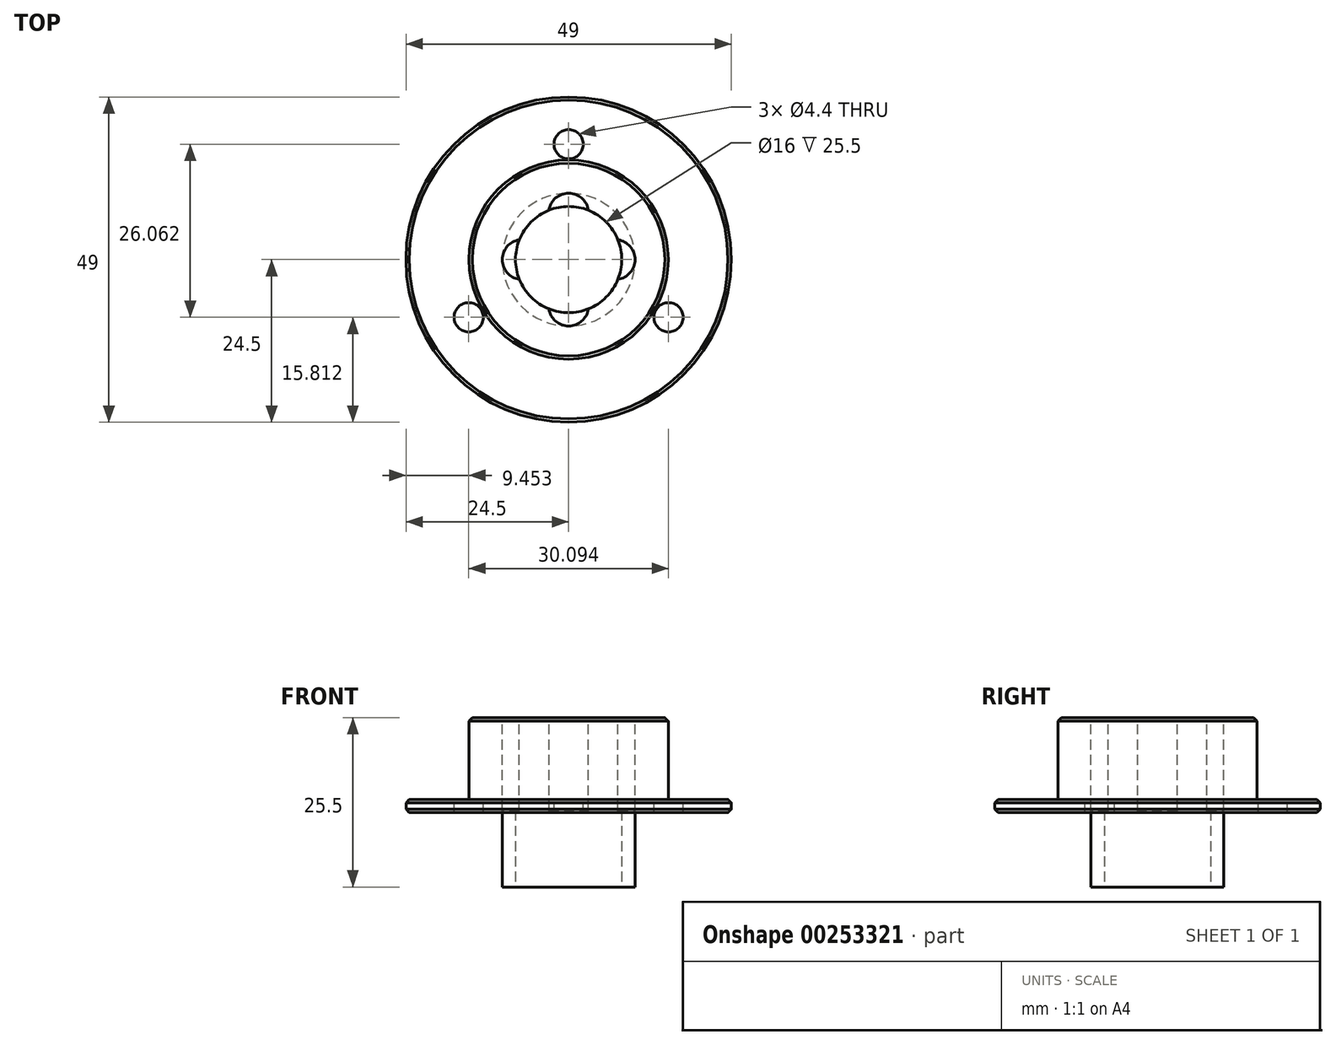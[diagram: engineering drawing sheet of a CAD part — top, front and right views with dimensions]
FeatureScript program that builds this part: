
annotation { "Feature Type Name" : "Feature", "Feature Type Description" : "" }
export const myFeature = defineFeature(function(context is Context, id is Id, definition is map)
    precondition{}
    {
        {
            var Q0;
            Q0=qCreatedBy(makeId("Top.planeOp"),FACE);
            var sketch = newSketch(context, id + "F0", { "sketchPlane" : qUnion([Q0])});
            skCircle(sketch, "E0", {"center": v(0, 0) * mm, "radius": 24.5 * mm});
            skCircle(sketch, "E1", {"center": v(0, 0) * mm, "radius": 15 * mm});
            skCircle(sketch, "E2", {"center": v(0, 0) * mm, "radius": 8 * mm});
            skSolve(sketch);
        }
        {
            var Q0;
            Q0=makeQuery(id+"F0.imprint","IMPRINT",FACE,{"disambiguationData":[TD([[makeQuery(id+"F0.imprint","IMPRINT",EDGE,{"derivedFrom":sQuery(id+"F0.wireOp",EDGE,"E1")}),1.0]])]});
            extrude(context, id + "F1", {"entities" : qUnion([Q0]), "depth" : 14.3 * mm});
        }
        {
            var Q0;
            Q0=makeQuery(id+"F0.imprint","IMPRINT",FACE,{"disambiguationData":[TD([[makeQuery(id+"F0.imprint","IMPRINT",EDGE,{"derivedFrom":sQuery(id+"F0.wireOp",EDGE,"E0")}),1.0]])]});
            extrude(context, id + "F2", {"entities" : qUnion([Q0]), "operationType" : NewBodyOperationType.ADD, "depth" : 2 * mm});
        }
        {
            var Q0;
            Q0=makeQuery(id+"F1.opExtrude","CAP_FACE",FACE,{"disambiguationData":[OSD([sQuery(id+"F0.wireOp",EDGE,"E1"),sQuery(id+"F0.wireOp",EDGE,"E2")])],"isStart":false});
            var sketch = newSketch(context, id + "F3", { "sketchPlane" : qUnion([Q0])});
            skCircle(sketch, "E3.0", {"center": v(0, 0) * mm, "radius": 8 * mm});
            skCircle(sketch, "E4", {"center": v(0, 0) * mm, "radius": 7 * mm, "construction": true});
            skCircle(sketch, "E5", {"center": v(0, 7) * mm, "radius": 3 * mm});
            skCircle(sketch, "E6.1.0", {"center": v(-7, 0) * mm, "radius": 3 * mm});
            skCircle(sketch, "E6.2.0", {"center": v(0, -7) * mm, "radius": 3 * mm});
            skCircle(sketch, "E6.3.0", {"center": v(7, 0) * mm, "radius": 3 * mm});
            skSolve(sketch);
        }
        {
            var Q0;
            Q0 = qSketchRegion(id + "F3", true);
            extrude(context, id + "F4", {"entities" : qUnion([Q0]), "operationType" : NewBodyOperationType.REMOVE, "oppositeDirection" : true, "depth" : 14 * mm});
        }
        {
            var Q0;
            Q0=makeQuery(id+"F2.opExtrude","CAP_FACE",FACE,{"disambiguationData":[OSD([sQuery(id+"F0.wireOp",EDGE,"E0"),sQuery(id+"F0.wireOp",EDGE,"E1")])],"isStart":false});
            var sketch = newSketch(context, id + "F5", { "sketchPlane" : qUnion([Q0])});
            skCircle(sketch, "E7", {"center": v(0, 0) * mm, "radius": 17.38 * mm, "construction": true});
            skPoint(sketch, "E8", {"position": v(0, 17.38) * mm});
            skPoint(sketch, "E9.1.0", {"position": v(-15.05, -8.69) * mm});
            skPoint(sketch, "E9.2.0", {"position": v(15.05, -8.69) * mm});
            skSolve(sketch);
        }
        {
            var Q0;
            Q0=sQuery(id+"F5.wireOp",VERTEX,"E8");
            var Q1;
            Q1=sQuery(id+"F5.wireOp",VERTEX,"E9.2.0");
            var Q2;
            Q2=sQuery(id+"F5.wireOp",VERTEX,"E9.1.0");
            var Q3;
            Q3=makeQuery(id+"F1.opExtrude","SWEPT_BODY",BODY,{"disambiguationData":[OSD([sQuery(id+"F0.wireOp",EDGE,"E1"),sQuery(id+"F0.wireOp",EDGE,"E2")])]});
            hole(context, id + "F6", {"style" : HoleStyle.SIMPLE, "endStyle" : HoleEndStyle.THROUGH, "standardTappedOrClearance" : lookupTablePath({ "standard" : "ISO", "fit" : "Normal", "size" : "M4", "type" : "Clearance" }), "standardBlindInLast" : lookupTablePath({ "fit" : "Standard", "standard" : "ISO", "size" : "M4", "type" : "Clearance" }), "holeDiameter" : 4.4 * mm, "tappedDepth" : 12 * mm, "tapClearance" : 3, "locations" : qUnion([Q0, Q1, Q2]), "scope" : qUnion([Q3])});
        }
        {
            var Q0;
            Q0=makeQuery(id+"F0.imprint","IMPRINT",FACE,{"disambiguationData":[TD([[makeQuery(id+"F0.imprint","IMPRINT",EDGE,{"derivedFrom":sQuery(id+"F0.wireOp",EDGE,"E0")}),1.0]])]});
            var sketch = newSketch(context, id + "F7", { "sketchPlane" : qUnion([Q0])});
            skPoint(sketch, "E10.0", {"position": v(0, 10) * mm});
            skCircle(sketch, "E11.0", {"center": v(0, 0) * mm, "radius": 8 * mm});
            skCircle(sketch, "E12", {"center": v(0, 0) * mm, "radius": 10 * mm});
            skSolve(sketch);
        }
        {
            var Q0;
            Q0 = qSketchRegion(id + "F7", true);
            extrude(context, id + "F8", {"entities" : qUnion([Q0]), "operationType" : NewBodyOperationType.ADD, "oppositeDirection" : true, "depth" : 11.2 * mm});
        }
        {
            var Q0;
            {var subQ0=sQuery(id+"F3.wireOp",EDGE,"E5");var subQ1=sQuery(id+"F3.wireOp",EDGE,"E3.0");Q0=makeQuery(id+"F4.boolean.opBoolean","COPY",EDGE,{"derivedFrom":makeQuery(id+"F4.opExtrude","SWEPT_EDGE",EDGE,{"disambiguationData":[OSD([subQ1,subQ0]),TDD([makeQuery(id+"F3.imprint","INTERSECT",VERTEX,{"disambiguationData":[OD(0.0)],"derivedFrom":[subQ1,subQ0]})])]})});}
            var Q1;
            {var subQ0=sQuery(id+"F3.wireOp",EDGE,"E6.3.0");var subQ1=sQuery(id+"F3.wireOp",EDGE,"E3.0");Q1=makeQuery(id+"F4.boolean.opBoolean","COPY",EDGE,{"derivedFrom":makeQuery(id+"F4.opExtrude","SWEPT_EDGE",EDGE,{"disambiguationData":[OSD([subQ1,subQ0]),TDD([makeQuery(id+"F3.imprint","INTERSECT",VERTEX,{"disambiguationData":[OD(0.0)],"derivedFrom":[subQ1,subQ0]})])]})});}
            var Q2;
            {var subQ0=sQuery(id+"F3.wireOp",EDGE,"E5");var subQ1=sQuery(id+"F3.wireOp",EDGE,"E3.0");Q2=makeQuery(id+"F4.boolean.opBoolean","COPY",EDGE,{"derivedFrom":makeQuery(id+"F4.opExtrude","SWEPT_EDGE",EDGE,{"disambiguationData":[OSD([subQ1,subQ0]),TDD([makeQuery(id+"F3.imprint","INTERSECT",VERTEX,{"disambiguationData":[OD(1.0)],"derivedFrom":[subQ1,subQ0]})])]})});}
            var Q3;
            {var subQ0=sQuery(id+"F3.wireOp",EDGE,"E6.1.0");var subQ1=sQuery(id+"F3.wireOp",EDGE,"E3.0");Q3=makeQuery(id+"F4.boolean.opBoolean","COPY",EDGE,{"derivedFrom":makeQuery(id+"F4.opExtrude","SWEPT_EDGE",EDGE,{"disambiguationData":[OSD([subQ1,subQ0]),TDD([makeQuery(id+"F3.imprint","INTERSECT",VERTEX,{"disambiguationData":[OD(0.0)],"derivedFrom":[subQ1,subQ0]})])]})});}
            var Q4;
            {var subQ0=sQuery(id+"F3.wireOp",EDGE,"E6.1.0");var subQ1=sQuery(id+"F3.wireOp",EDGE,"E3.0");Q4=makeQuery(id+"F4.boolean.opBoolean","COPY",EDGE,{"derivedFrom":makeQuery(id+"F4.opExtrude","SWEPT_EDGE",EDGE,{"disambiguationData":[OSD([subQ1,subQ0]),TDD([makeQuery(id+"F3.imprint","INTERSECT",VERTEX,{"disambiguationData":[OD(1.0)],"derivedFrom":[subQ1,subQ0]})])]})});}
            var Q5;
            {var subQ0=sQuery(id+"F3.wireOp",EDGE,"E6.2.0");var subQ1=sQuery(id+"F3.wireOp",EDGE,"E3.0");Q5=makeQuery(id+"F4.boolean.opBoolean","COPY",EDGE,{"derivedFrom":makeQuery(id+"F4.opExtrude","SWEPT_EDGE",EDGE,{"disambiguationData":[OSD([subQ1,subQ0]),TDD([makeQuery(id+"F3.imprint","INTERSECT",VERTEX,{"disambiguationData":[OD(0.0)],"derivedFrom":[subQ1,subQ0]})])]})});}
            var Q6;
            {var subQ0=sQuery(id+"F3.wireOp",EDGE,"E6.2.0");var subQ1=sQuery(id+"F3.wireOp",EDGE,"E3.0");Q6=makeQuery(id+"F4.boolean.opBoolean","COPY",EDGE,{"derivedFrom":makeQuery(id+"F4.opExtrude","SWEPT_EDGE",EDGE,{"disambiguationData":[OSD([subQ1,subQ0]),TDD([makeQuery(id+"F3.imprint","INTERSECT",VERTEX,{"disambiguationData":[OD(1.0)],"derivedFrom":[subQ1,subQ0]})])]})});}
            var Q7;
            {var subQ0=sQuery(id+"F3.wireOp",EDGE,"E6.3.0");var subQ1=sQuery(id+"F3.wireOp",EDGE,"E3.0");Q7=makeQuery(id+"F4.boolean.opBoolean","COPY",EDGE,{"derivedFrom":makeQuery(id+"F4.opExtrude","SWEPT_EDGE",EDGE,{"disambiguationData":[OSD([subQ1,subQ0]),TDD([makeQuery(id+"F3.imprint","INTERSECT",VERTEX,{"disambiguationData":[OD(1.0)],"derivedFrom":[subQ1,subQ0]})])]})});}
            var Q8;
            Q8=makeQuery(id+"F1.opExtrude","CAP_EDGE",EDGE,{"disambiguationData":[OSD([sQuery(id+"F0.wireOp",EDGE,"E1")])],"isStart":false});
            chamfer(context, id + "F9", {"entities" : qUnion([Q0, Q1, Q2, Q3, Q4, Q5, Q6, Q7, Q8]), "chamferType" : ChamferType.OFFSET_ANGLE, "width" : .5 * mm, "oppositeDirection" : false, "angle" : 45 * degree, "tangentPropagation" : true});
        }
        {
            var Q0;
            Q0=makeQuery(id+"F2.opExtrude","CAP_EDGE",EDGE,{"disambiguationData":[OSD([sQuery(id+"F0.wireOp",EDGE,"E0")])],"isStart":false});
            var Q1;
            Q1=makeQuery(id+"F2.opExtrude","CAP_EDGE",EDGE,{"disambiguationData":[OSD([sQuery(id+"F0.wireOp",EDGE,"E0")])],"isStart":true});
            chamfer(context, id + "F10", {"entities" : qUnion([Q0, Q1]), "chamferType" : ChamferType.OFFSET_ANGLE, "width" : .5 * mm, "oppositeDirection" : false, "angle" : 45 * degree, "tangentPropagation" : true});
        }
    });
